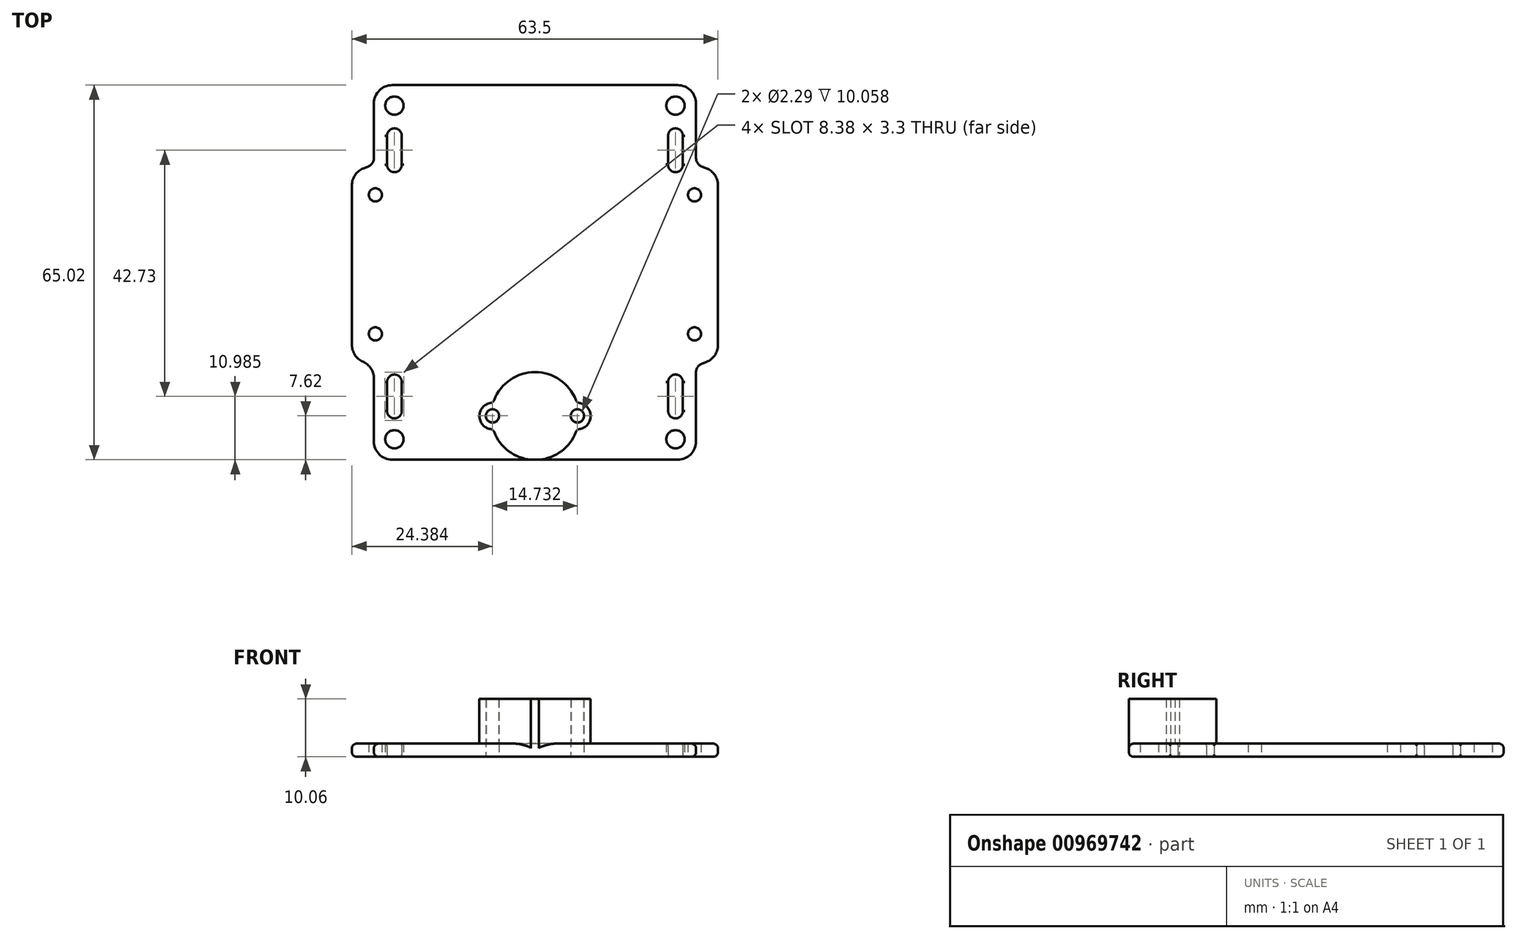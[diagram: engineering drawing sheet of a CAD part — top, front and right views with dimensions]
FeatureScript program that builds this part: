
annotation { "Feature Type Name" : "Feature", "Feature Type Description" : "" }
export const myFeature = defineFeature(function(context is Context, id is Id, definition is map)
    precondition{}
    {
        {
            var Q0;
            Q0=qCreatedBy(makeId("Top.planeOp"),FACE);
            var sketch = newSketch(context, id + "F0", { "sketchPlane" : qUnion([Q0])});
            skLineSegment(sketch, "E0", {"start": v(0, -32.35) * mm, "end": v(-27.94, -32.35) * mm});
            skLineSegment(sketch, "E1", {"start": v(-27.94, -32.35) * mm, "end": v(-27.94, -16.1) * mm});
            skLineSegment(sketch, "E2", {"start": v(-27.94, -16.1) * mm, "end": v(-31.75, -14.57) * mm});
            skLineSegment(sketch, "E3", {"start": v(-31.75, -14.57) * mm, "end": v(-31.75, 17.43) * mm});
            skLineSegment(sketch, "E4", {"start": v(-31.75, 17.43) * mm, "end": v(-27.94, 18.96) * mm});
            skLineSegment(sketch, "E5", {"start": v(-27.94, 18.96) * mm, "end": v(-27.94, 32.67) * mm});
            skLineSegment(sketch, "E6", {"start": v(-27.94, 32.67) * mm, "end": v(27.94, 32.67) * mm});
            skLineSegment(sketch, "E7", {"start": v(27.94, 32.67) * mm, "end": v(27.94, 18.96) * mm});
            skLineSegment(sketch, "E8", {"start": v(27.94, 18.96) * mm, "end": v(31.75, 17.43) * mm});
            skLineSegment(sketch, "E9", {"start": v(31.75, 17.43) * mm, "end": v(31.75, -14.57) * mm});
            skLineSegment(sketch, "E10", {"start": v(31.75, -14.57) * mm, "end": v(27.94, -16.1) * mm});
            skLineSegment(sketch, "E11", {"start": v(27.94, -16.1) * mm, "end": v(27.94, -32.35) * mm});
            skLineSegment(sketch, "E12", {"start": v(27.94, -32.35) * mm, "end": v(0, -32.35) * mm});
            skLineSegment(sketch, "E13", {"start": v(0, -32.35) * mm, "end": v(0, 32.67) * mm, "construction": true});
            skLineSegment(sketch, "E14", {"start": v(-29.38, 29.12) * mm, "end": v(30.41, 29.12) * mm, "construction": true});
            skLineSegment(sketch, "E15", {"start": v(-30.17, -28.8) * mm, "end": v(31.36, -28.8) * mm, "construction": true});
            skLineSegment(sketch, "E16", {"start": v(-24.38, 34.73) * mm, "end": v(-24.38, -35.44) * mm, "construction": true});
            skLineSegment(sketch, "E17", {"start": v(24.38, 35.22) * mm, "end": v(24.38, -36.91) * mm, "construction": true});
            skCircle(sketch, "E18", {"center": v(-24.38, 29.12) * mm, "radius": 1.59 * mm});
            skCircle(sketch, "E19", {"center": v(24.38, 29.12) * mm, "radius": 1.59 * mm});
            skCircle(sketch, "E20", {"center": v(-24.38, -28.8) * mm, "radius": 1.59 * mm});
            skCircle(sketch, "E21", {"center": v(24.38, -28.8) * mm, "radius": 1.59 * mm});
            skLineSegment(sketch, "E22", {"start": v(-27.69, 13.62) * mm, "end": v(-27.69, -10.5) * mm, "construction": true});
            skCircle(sketch, "E23", {"center": v(-27.69, 13.62) * mm, "radius": 1.14 * mm});
            skCircle(sketch, "E24", {"center": v(-27.69, -10.5) * mm, "radius": 1.14 * mm});
            skCircle(sketch, "E25.MirrorC", {"center": v(27.69, 13.62) * mm, "radius": 1.14 * mm});
            skCircle(sketch, "E26.MirrorC", {"center": v(27.69, -10.5) * mm, "radius": 1.14 * mm});
            skLineSegment(sketch, "E27", {"start": v(0, -24.73) * mm, "end": v(-7.37, -24.73) * mm});
            skCircle(sketch, "E28", {"center": v(0, -24.73) * mm, "radius": 7.62 * mm});
            skCircle(sketch, "E29", {"center": v(-7.37, -24.73) * mm, "radius": 1.14 * mm});
            skCircle(sketch, "E30", {"center": v(-7.37, -24.73) * mm, "radius": 2.29 * mm});
            skCircle(sketch, "E31.MirrorC", {"center": v(7.37, -24.73) * mm, "radius": 1.14 * mm});
            skCircle(sketch, "E32.MirrorC", {"center": v(7.37, -24.73) * mm, "radius": 2.29 * mm});
            skArc(sketch, "E33", {"start": v(-25.65, -23.85) * mm, "mid": v(-24.4, -25.17) * mm, "end": v(-23.11, -23.9) * mm});
            skArc(sketch, "E34", {"start": v(-23.12, -18.88) * mm, "mid": v(-24.38, -17.55) * mm, "end": v(-25.65, -18.88) * mm});
            skLineSegment(sketch, "E35", {"start": v(-25.65, -18.77) * mm, "end": v(-25.65, -23.96) * mm});
            skLineSegment(sketch, "E36", {"start": v(-23.12, -18.77) * mm, "end": v(-23.11, -23.9) * mm});
            skArc(sketch, "E37.MirrorCS", {"start": v(23.12, -18.88) * mm, "mid": v(24.38, -17.55) * mm, "end": v(25.65, -18.88) * mm});
            skArc(sketch, "E38.MirrorCS", {"start": v(25.65, -23.85) * mm, "mid": v(24.4, -25.17) * mm, "end": v(23.11, -23.9) * mm});
            skLineSegment(sketch, "E39.MirrorCS", {"start": v(23.12, -18.77) * mm, "end": v(23.11, -23.9) * mm});
            skLineSegment(sketch, "E40.MirrorCS", {"start": v(25.65, -18.77) * mm, "end": v(25.65, -23.96) * mm});
            skPoint(sketch, "E41.orphan", {"position": v(-24.38, -22.63) * mm});
            skPoint(sketch, "E42.orphan", {"position": v(24.38, -22.63) * mm});
            skArc(sketch, "E43.MirrorCS", {"start": v(23.12, 18.88) * mm, "mid": v(24.38, 17.55) * mm, "end": v(25.65, 18.88) * mm});
            skLineSegment(sketch, "E44.MirrorCS", {"start": v(23.12, 18.77) * mm, "end": v(23.11, 23.9) * mm});
            skArc(sketch, "E45.MirrorCS", {"start": v(25.65, 23.85) * mm, "mid": v(24.4, 25.17) * mm, "end": v(23.11, 23.9) * mm});
            skLineSegment(sketch, "E46.MirrorCS", {"start": v(25.65, 18.77) * mm, "end": v(25.65, 23.96) * mm});
            skArc(sketch, "E47.MirrorCS", {"start": v(-25.65, 23.85) * mm, "mid": v(-24.4, 25.17) * mm, "end": v(-23.11, 23.9) * mm});
            skLineSegment(sketch, "E48.MirrorCS", {"start": v(-23.12, 18.77) * mm, "end": v(-23.11, 23.9) * mm});
            skArc(sketch, "E49.MirrorCS", {"start": v(-23.12, 18.88) * mm, "mid": v(-24.38, 17.55) * mm, "end": v(-25.65, 18.88) * mm});
            skLineSegment(sketch, "E50.MirrorCS", {"start": v(-25.65, 18.77) * mm, "end": v(-25.65, 23.96) * mm});
            skSolve(sketch);
        }
        {
            var Q0;
            {var subQ6=sQuery(id+"F0.wireOp",EDGE,"E0");Q0=makeQuery(id+"F0.imprint","IMPRINT",FACE,{"disambiguationData":[TD([[makeQuery(id+"F0.imprint","IMPRINT",EDGE,{"derivedFrom":subQ6}),-1.0]])]});}
            var Q1;
            {var subQ2=sQuery(id+"F0.wireOp",EDGE,"E28");var subQ4=sQuery(id+"F0.wireOp",EDGE,"E32.MirrorC");var subQ5=makeQuery(id+"F0.imprint","INTERSECT",VERTEX,{"disambiguationData":[OD(0.0)],"derivedFrom":[subQ2,subQ4]});Q1=makeQuery(id+"F0.imprint","IMPRINT",FACE,{"disambiguationData":[TD([[makeQuery(id+"F0.imprint","IMPRINT",EDGE,{"disambiguationData":[TD([[subQ5,-1.0]])],"derivedFrom":subQ2}),1.0]])]});}
            var Q2;
            {var subQ0=sQuery(id+"F0.wireOp",EDGE,"E29");var subQ1=sQuery(id+"F0.wireOp",EDGE,"E27");var subQ2=makeQuery(id+"F0.imprint","INTERSECT",VERTEX,{"derivedFrom":[subQ1,subQ0]});Q2=makeQuery(id+"F0.imprint","IMPRINT",FACE,{"disambiguationData":[TD([[makeQuery(id+"F0.imprint","IMPRINT",EDGE,{"disambiguationData":[TD([[subQ2,1.0]])],"derivedFrom":subQ1}),-1.0]])]});}
            var Q3;
            {var subQ0=sQuery(id+"F0.wireOp",EDGE,"E30");var subQ1=sQuery(id+"F0.wireOp",EDGE,"E28");var subQ2=makeQuery(id+"F0.imprint","INTERSECT",VERTEX,{"disambiguationData":[OD(0.0)],"derivedFrom":[subQ1,subQ0]});Q3=makeQuery(id+"F0.imprint","IMPRINT",FACE,{"disambiguationData":[TD([[makeQuery(id+"F0.imprint","IMPRINT",EDGE,{"disambiguationData":[TD([[subQ2,-1.0]])],"derivedFrom":subQ1}),-1.0]])]});}
            var Q4;
            {var subQ0=sQuery(id+"F0.wireOp",EDGE,"E29");var subQ1=sQuery(id+"F0.wireOp",EDGE,"E27");var subQ2=makeQuery(id+"F0.imprint","INTERSECT",VERTEX,{"derivedFrom":[subQ1,subQ0]});Q4=makeQuery(id+"F0.imprint","IMPRINT",FACE,{"disambiguationData":[TD([[makeQuery(id+"F0.imprint","IMPRINT",EDGE,{"disambiguationData":[TD([[subQ2,1.0]])],"derivedFrom":subQ1}),1.0]])]});}
            var Q5;
            {var subQ0=sQuery(id+"F0.wireOp",EDGE,"E32.MirrorC");var subQ1=sQuery(id+"F0.wireOp",EDGE,"E28");var subQ2=makeQuery(id+"F0.imprint","INTERSECT",VERTEX,{"disambiguationData":[OD(0.0)],"derivedFrom":[subQ1,subQ0]});Q5=makeQuery(id+"F0.imprint","IMPRINT",FACE,{"disambiguationData":[TD([[makeQuery(id+"F0.imprint","IMPRINT",EDGE,{"disambiguationData":[TD([[subQ2,1.0]])],"derivedFrom":subQ1}),-1.0]])]});}
            var Q6;
            {var subQ0=sQuery(id+"F0.wireOp",EDGE,"E32.MirrorC");var subQ1=sQuery(id+"F0.wireOp",EDGE,"E28");var subQ2=makeQuery(id+"F0.imprint","INTERSECT",VERTEX,{"disambiguationData":[OD(0.0)],"derivedFrom":[subQ1,subQ0]});Q6=makeQuery(id+"F0.imprint","IMPRINT",FACE,{"disambiguationData":[TD([[makeQuery(id+"F0.imprint","IMPRINT",EDGE,{"disambiguationData":[TD([[subQ2,1.0]])],"derivedFrom":subQ1}),1.0]])]});}
            extrude(context, id + "F1", {"entities" : qUnion([Q0, Q1, Q2, Q3, Q4, Q5, Q6]), "depth" : 2.3 * mm, "offsetDistance" : 25.4 * mm});
        }
        {
            var Q0;
            Q0=makeQuery(id+"F1.opExtrude","CAP_FACE",FACE,{"disambiguationData":[OSD([sQuery(id+"F0.wireOp",EDGE,"E0"),sQuery(id+"F0.wireOp",EDGE,"E1"),sQuery(id+"F0.wireOp",EDGE,"E2"),sQuery(id+"F0.wireOp",EDGE,"E3"),sQuery(id+"F0.wireOp",EDGE,"E4"),sQuery(id+"F0.wireOp",EDGE,"E5"),sQuery(id+"F0.wireOp",EDGE,"E6"),sQuery(id+"F0.wireOp",EDGE,"E7"),sQuery(id+"F0.wireOp",EDGE,"E8"),sQuery(id+"F0.wireOp",EDGE,"E9"),sQuery(id+"F0.wireOp",EDGE,"E10"),sQuery(id+"F0.wireOp",EDGE,"E11"),sQuery(id+"F0.wireOp",EDGE,"E12"),sQuery(id+"F0.wireOp",EDGE,"E18"),sQuery(id+"F0.wireOp",EDGE,"E19"),sQuery(id+"F0.wireOp",EDGE,"E20"),sQuery(id+"F0.wireOp",EDGE,"E21"),sQuery(id+"F0.wireOp",EDGE,"E23"),sQuery(id+"F0.wireOp",EDGE,"E24"),sQuery(id+"F0.wireOp",EDGE,"E25.MirrorC"),sQuery(id+"F0.wireOp",EDGE,"E26.MirrorC"),sQuery(id+"F0.wireOp",EDGE,"E29"),sQuery(id+"F0.wireOp",EDGE,"E31.MirrorC")])],"isStart":false});
            var sketch = newSketch(context, id + "F2", { "sketchPlane" : qUnion([Q0])});
            skCircle(sketch, "E51", {"center": v(0.01, -24.76) * mm, "radius": 7.62 * mm});
            skCircle(sketch, "E52", {"center": v(-7.35, -24.76) * mm, "radius": 1.14 * mm});
            skCircle(sketch, "E53", {"center": v(-7.35, -24.76) * mm, "radius": 2.29 * mm});
            skCircle(sketch, "E54.MirrorC", {"center": v(7.38, -24.76) * mm, "radius": 1.14 * mm});
            skCircle(sketch, "E55.MirrorC", {"center": v(7.38, -24.76) * mm, "radius": 2.29 * mm});
            skSolve(sketch);
        }
        {
            var Q0;
            {var subQ1=sQuery(id+"F2.wireOp",EDGE,"E51");var subQ6=sQuery(id+"F2.wireOp",EDGE,"E53");var subQ8=makeQuery(id+"F2.imprint","INTERSECT",VERTEX,{"disambiguationData":[OD(0.0)],"derivedFrom":[subQ1,subQ6]});Q0=makeQuery(id+"F2.imprint","IMPRINT",FACE,{"disambiguationData":[TD([[makeQuery(id+"F2.imprint","IMPRINT",EDGE,{"disambiguationData":[TD([[subQ8,-1.0]])],"derivedFrom":subQ1}),-1.0]])]});}
            var Q1;
            {var subQ0=sQuery(id+"F2.wireOp",EDGE,"E53");var subQ1=sQuery(id+"F2.wireOp",EDGE,"E51");var subQ2=makeQuery(id+"F2.imprint","INTERSECT",VERTEX,{"disambiguationData":[OD(0.0)],"derivedFrom":[subQ1,subQ0]});Q1=makeQuery(id+"F2.imprint","IMPRINT",FACE,{"disambiguationData":[TD([[makeQuery(id+"F2.imprint","IMPRINT",EDGE,{"disambiguationData":[TD([[subQ2,-1.0]])],"derivedFrom":subQ1}),1.0]])]});}
            var Q2;
            {var subQ1=sQuery(id+"F2.wireOp",EDGE,"E51");var subQ6=sQuery(id+"F2.wireOp",EDGE,"E55.MirrorC");var subQ9=makeQuery(id+"F2.imprint","INTERSECT",VERTEX,{"disambiguationData":[OD(0.0)],"derivedFrom":[subQ1,subQ6]});Q2=makeQuery(id+"F2.imprint","IMPRINT",FACE,{"disambiguationData":[TD([[makeQuery(id+"F2.imprint","IMPRINT",EDGE,{"disambiguationData":[TD([[subQ9,-1.0]])],"derivedFrom":subQ1}),1.0]])]});}
            var Q3;
            {var subQ0=sQuery(id+"F2.wireOp",EDGE,"E55.MirrorC");var subQ1=sQuery(id+"F2.wireOp",EDGE,"E51");var subQ2=makeQuery(id+"F2.imprint","INTERSECT",VERTEX,{"disambiguationData":[OD(0.0)],"derivedFrom":[subQ1,subQ0]});Q3=makeQuery(id+"F2.imprint","IMPRINT",FACE,{"disambiguationData":[TD([[makeQuery(id+"F2.imprint","IMPRINT",EDGE,{"disambiguationData":[TD([[subQ2,1.0]])],"derivedFrom":subQ1}),1.0]])]});}
            var Q4;
            {var subQ0=sQuery(id+"F2.wireOp",EDGE,"E55.MirrorC");var subQ1=sQuery(id+"F2.wireOp",EDGE,"E51");var subQ2=makeQuery(id+"F2.imprint","INTERSECT",VERTEX,{"disambiguationData":[OD(0.0)],"derivedFrom":[subQ1,subQ0]});Q4=makeQuery(id+"F2.imprint","IMPRINT",FACE,{"disambiguationData":[TD([[makeQuery(id+"F2.imprint","IMPRINT",EDGE,{"disambiguationData":[TD([[subQ2,1.0]])],"derivedFrom":subQ1}),-1.0]])]});}
            extrude(context, id + "F3", {"entities" : qUnion([Q0, Q1, Q2, Q3, Q4]), "operationType" : NewBodyOperationType.ADD, "depth" : 7.77 * mm, "offsetDistance" : 25.4 * mm});
        }
        {
            var Q0;
            {var subQ0=sQuery(id+"F2.wireOp",EDGE,"E53");var subQ1=sQuery(id+"F2.wireOp",EDGE,"E51");Q0=makeQuery(id+"F3.opExtrude","SWEPT_EDGE",EDGE,{"disambiguationData":[OSD([subQ1,subQ0]),TDD([makeQuery(id+"F2.imprint","INTERSECT",VERTEX,{"disambiguationData":[OD(1.0)],"derivedFrom":[subQ1,subQ0]})])]});}
            var Q1;
            {var subQ0=sQuery(id+"F2.wireOp",EDGE,"E51");Q1=makeQuery(id+"F3.opExtrude","CAP_EDGE",EDGE,{"disambiguationData":[OSD([subQ0]),TDD([makeQuery(id+"F2.imprint","IMPRINT",EDGE,{"disambiguationData":[TD([[makeQuery(id+"F2.imprint","INTERSECT",VERTEX,{"disambiguationData":[OD(1.0)],"derivedFrom":[subQ0,sQuery(id+"F2.wireOp",EDGE,"E53")]}),-1.0]])],"derivedFrom":subQ0})])],"isStart":true});}
            var Q2;
            Q2=makeQuery(id+"F3.opExtrude","CAP_EDGE",EDGE,{"disambiguationData":[OSD([sQuery(id+"F2.wireOp",EDGE,"E53")])],"isStart":true});
            var Q3;
            {var subQ0=sQuery(id+"F2.wireOp",EDGE,"E53");var subQ1=sQuery(id+"F2.wireOp",EDGE,"E51");Q3=makeQuery(id+"F3.opExtrude","SWEPT_EDGE",EDGE,{"disambiguationData":[OSD([subQ1,subQ0]),TDD([makeQuery(id+"F2.imprint","INTERSECT",VERTEX,{"disambiguationData":[OD(0.0)],"derivedFrom":[subQ1,subQ0]})])]});}
            var Q4;
            {var subQ0=sQuery(id+"F2.wireOp",EDGE,"E51");Q4=makeQuery(id+"F3.opExtrude","CAP_EDGE",EDGE,{"disambiguationData":[OSD([subQ0]),TDD([makeQuery(id+"F2.imprint","IMPRINT",EDGE,{"disambiguationData":[TD([[makeQuery(id+"F2.imprint","INTERSECT",VERTEX,{"disambiguationData":[OD(0.0)],"derivedFrom":[subQ0,sQuery(id+"F2.wireOp",EDGE,"E55.MirrorC")]}),-1.0]])],"derivedFrom":subQ0})])],"isStart":true});}
            var Q5;
            {var subQ0=sQuery(id+"F2.wireOp",EDGE,"E55.MirrorC");var subQ1=sQuery(id+"F2.wireOp",EDGE,"E51");Q5=makeQuery(id+"F3.opExtrude","SWEPT_EDGE",EDGE,{"disambiguationData":[OSD([subQ1,subQ0]),TDD([makeQuery(id+"F2.imprint","INTERSECT",VERTEX,{"disambiguationData":[OD(0.0)],"derivedFrom":[subQ1,subQ0]})])]});}
            var Q6;
            Q6=makeQuery(id+"F3.opExtrude","CAP_EDGE",EDGE,{"disambiguationData":[OSD([sQuery(id+"F2.wireOp",EDGE,"E55.MirrorC")])],"isStart":true});
            var Q7;
            {var subQ0=sQuery(id+"F2.wireOp",EDGE,"E55.MirrorC");var subQ1=sQuery(id+"F2.wireOp",EDGE,"E51");Q7=makeQuery(id+"F3.opExtrude","SWEPT_EDGE",EDGE,{"disambiguationData":[OSD([subQ1,subQ0]),TDD([makeQuery(id+"F2.imprint","INTERSECT",VERTEX,{"disambiguationData":[OD(1.0)],"derivedFrom":[subQ1,subQ0]})])]});}
            var Q8;
            {var subQ0=sQuery(id+"F2.wireOp",EDGE,"E51");Q8=makeQuery(id+"F3.opExtrude","CAP_EDGE",EDGE,{"disambiguationData":[OSD([subQ0]),TDD([makeQuery(id+"F2.imprint","IMPRINT",EDGE,{"disambiguationData":[TD([[makeQuery(id+"F2.imprint","INTERSECT",VERTEX,{"disambiguationData":[OD(1.0)],"derivedFrom":[subQ0,sQuery(id+"F2.wireOp",EDGE,"E55.MirrorC")]}),1.0]])],"derivedFrom":subQ0})])],"isStart":true});}
            fillet(context, id + "F4", {"entities" : qUnion([Q0, Q1, Q2, Q3, Q4, Q5, Q6, Q7, Q8]), "radius" : 0.81 * mm, "tangentPropagation" : true, "allowEdgeOverflow" : false});
        }
        {
            var Q0;
            Q0=makeQuery(id+"F1.opExtrude","SWEPT_EDGE",EDGE,{"disambiguationData":[OSD([sQuery(id+"F0.wireOp",EDGE,"E6"),sQuery(id+"F0.wireOp",EDGE,"E7")])]});
            var Q1;
            Q1=makeQuery(id+"F1.opExtrude","SWEPT_EDGE",EDGE,{"disambiguationData":[OSD([sQuery(id+"F0.wireOp",EDGE,"E5"),sQuery(id+"F0.wireOp",EDGE,"E6")])]});
            var Q2;
            Q2=makeQuery(id+"F1.opExtrude","SWEPT_EDGE",EDGE,{"disambiguationData":[OSD([sQuery(id+"F0.wireOp",EDGE,"E0"),sQuery(id+"F0.wireOp",EDGE,"E1")])]});
            var Q3;
            Q3=makeQuery(id+"F1.opExtrude","SWEPT_EDGE",EDGE,{"disambiguationData":[OSD([sQuery(id+"F0.wireOp",EDGE,"E11"),sQuery(id+"F0.wireOp",EDGE,"E12")])]});
            var Q4;
            Q4=makeQuery(id+"F1.opExtrude","SWEPT_EDGE",EDGE,{"disambiguationData":[OSD([sQuery(id+"F0.wireOp",EDGE,"E2"),sQuery(id+"F0.wireOp",EDGE,"E3")])]});
            var Q5;
            Q5=makeQuery(id+"F1.opExtrude","SWEPT_EDGE",EDGE,{"disambiguationData":[OSD([sQuery(id+"F0.wireOp",EDGE,"E3"),sQuery(id+"F0.wireOp",EDGE,"E4")])]});
            var Q6;
            Q6=makeQuery(id+"F1.opExtrude","SWEPT_EDGE",EDGE,{"disambiguationData":[OSD([sQuery(id+"F0.wireOp",EDGE,"E9"),sQuery(id+"F0.wireOp",EDGE,"E10")])]});
            var Q7;
            Q7=makeQuery(id+"F1.opExtrude","SWEPT_EDGE",EDGE,{"disambiguationData":[OSD([sQuery(id+"F0.wireOp",EDGE,"E8"),sQuery(id+"F0.wireOp",EDGE,"E9")])]});
            fillet(context, id + "F5", {"entities" : qUnion([Q0, Q1, Q2, Q3, Q4, Q5, Q6, Q7]), "radius" : 3.17 * mm, "tangentPropagation" : true, "allowEdgeOverflow" : false});
        }
        {
            var Q0;
            Q0=makeQuery(id+"F1.opExtrude","SWEPT_EDGE",EDGE,{"disambiguationData":[OSD([sQuery(id+"F0.wireOp",EDGE,"E3"),sQuery(id+"F0.wireOp",EDGE,"E4")])]});
            var Q1;
            Q1=makeQuery(id+"F1.opExtrude","SWEPT_EDGE",EDGE,{"disambiguationData":[OSD([sQuery(id+"F0.wireOp",EDGE,"E1"),sQuery(id+"F0.wireOp",EDGE,"E2")])]});
            var Q2;
            Q2=makeQuery(id+"F1.opExtrude","SWEPT_EDGE",EDGE,{"disambiguationData":[OSD([sQuery(id+"F0.wireOp",EDGE,"E8"),sQuery(id+"F0.wireOp",EDGE,"E9")])]});
            var Q3;
            Q3=makeQuery(id+"F1.opExtrude","SWEPT_EDGE",EDGE,{"disambiguationData":[OSD([sQuery(id+"F0.wireOp",EDGE,"E9"),sQuery(id+"F0.wireOp",EDGE,"E10")])]});
            fillet(context, id + "F6", {"entities" : qUnion([Q0, Q1, Q2, Q3]), "radius" : 3.17 * mm, "tangentPropagation" : true, "allowEdgeOverflow" : false});
        }
        {
            var Q0;
            Q0=makeQuery(id+"F1.opExtrude","SWEPT_EDGE",EDGE,{"disambiguationData":[OSD([sQuery(id+"F0.wireOp",EDGE,"E4"),sQuery(id+"F0.wireOp",EDGE,"E5")])]});
            var Q1;
            Q1=makeQuery(id+"F1.opExtrude","SWEPT_EDGE",EDGE,{"disambiguationData":[OSD([sQuery(id+"F0.wireOp",EDGE,"E7"),sQuery(id+"F0.wireOp",EDGE,"E8")])]});
            var Q2;
            Q2=makeQuery(id+"F1.opExtrude","SWEPT_EDGE",EDGE,{"disambiguationData":[OSD([sQuery(id+"F0.wireOp",EDGE,"E10"),sQuery(id+"F0.wireOp",EDGE,"E11")])]});
            fillet(context, id + "F7", {"entities" : qUnion([Q0, Q1, Q2]), "radius" : 1.57 * mm, "tangentPropagation" : true, "allowEdgeOverflow" : false});
        }
        {
            var Q0;
            Q0=makeQuery(id+"F1.opExtrude","SWEPT_FACE",FACE,{"disambiguationData":[OSD([sQuery(id+"F0.wireOp",EDGE,"E9")])]});
            fillet(context, id + "F8", {"entities" : qUnion([Q0]), "radius" : 0.81 * mm, "tangentPropagation" : true, "allowEdgeOverflow" : false});
        }
        {
            var Q0;
            Q0=makeQuery(id+"F1.opExtrude","CAP_EDGE",EDGE,{"disambiguationData":[OSD([sQuery(id+"F0.wireOp",EDGE,"E44.MirrorCS")])],"isStart":false});
            var Q1;
            Q1=makeQuery(id+"F1.opExtrude","CAP_EDGE",EDGE,{"disambiguationData":[OSD([sQuery(id+"F0.wireOp",EDGE,"E43.MirrorCS")])],"isStart":false});
            var Q2;
            Q2=makeQuery(id+"F1.opExtrude","CAP_EDGE",EDGE,{"disambiguationData":[OSD([sQuery(id+"F0.wireOp",EDGE,"E46.MirrorCS")])],"isStart":false});
            var Q3;
            Q3=makeQuery(id+"F1.opExtrude","CAP_EDGE",EDGE,{"disambiguationData":[OSD([sQuery(id+"F0.wireOp",EDGE,"E47.MirrorCS")])],"isStart":false});
            var Q4;
            Q4=makeQuery(id+"F1.opExtrude","CAP_EDGE",EDGE,{"disambiguationData":[OSD([sQuery(id+"F0.wireOp",EDGE,"E48.MirrorCS")])],"isStart":false});
            var Q5;
            Q5=makeQuery(id+"F1.opExtrude","CAP_EDGE",EDGE,{"disambiguationData":[OSD([sQuery(id+"F0.wireOp",EDGE,"E49.MirrorCS")])],"isStart":false});
            var Q6;
            Q6=makeQuery(id+"F1.opExtrude","CAP_EDGE",EDGE,{"disambiguationData":[OSD([sQuery(id+"F0.wireOp",EDGE,"E50.MirrorCS")])],"isStart":false});
            var Q7;
            Q7=makeQuery(id+"F1.opExtrude","CAP_EDGE",EDGE,{"disambiguationData":[OSD([sQuery(id+"F0.wireOp",EDGE,"E36")])],"isStart":false});
            var Q8;
            Q8=makeQuery(id+"F1.opExtrude","CAP_EDGE",EDGE,{"disambiguationData":[OSD([sQuery(id+"F0.wireOp",EDGE,"E34")])],"isStart":false});
            var Q9;
            Q9=makeQuery(id+"F1.opExtrude","CAP_EDGE",EDGE,{"disambiguationData":[OSD([sQuery(id+"F0.wireOp",EDGE,"E35")])],"isStart":false});
            var Q10;
            Q10=makeQuery(id+"F1.opExtrude","CAP_EDGE",EDGE,{"disambiguationData":[OSD([sQuery(id+"F0.wireOp",EDGE,"E33")])],"isStart":false});
            var Q11;
            Q11=makeQuery(id+"F1.opExtrude","CAP_EDGE",EDGE,{"disambiguationData":[OSD([sQuery(id+"F0.wireOp",EDGE,"E37.MirrorCS")])],"isStart":false});
            var Q12;
            Q12=makeQuery(id+"F1.opExtrude","CAP_EDGE",EDGE,{"disambiguationData":[OSD([sQuery(id+"F0.wireOp",EDGE,"E40.MirrorCS")])],"isStart":false});
            var Q13;
            Q13=makeQuery(id+"F1.opExtrude","CAP_EDGE",EDGE,{"disambiguationData":[OSD([sQuery(id+"F0.wireOp",EDGE,"E39.MirrorCS")])],"isStart":false});
            var Q14;
            Q14=makeQuery(id+"F1.opExtrude","CAP_EDGE",EDGE,{"disambiguationData":[OSD([sQuery(id+"F0.wireOp",EDGE,"E38.MirrorCS")])],"isStart":false});
            var Q15;
            Q15=makeQuery(id+"F1.opExtrude","CAP_EDGE",EDGE,{"disambiguationData":[OSD([sQuery(id+"F0.wireOp",EDGE,"E49.MirrorCS")])],"isStart":true});
            var Q16;
            Q16=makeQuery(id+"F1.opExtrude","CAP_EDGE",EDGE,{"disambiguationData":[OSD([sQuery(id+"F0.wireOp",EDGE,"E50.MirrorCS")])],"isStart":true});
            var Q17;
            Q17=makeQuery(id+"F1.opExtrude","CAP_EDGE",EDGE,{"disambiguationData":[OSD([sQuery(id+"F0.wireOp",EDGE,"E47.MirrorCS")])],"isStart":true});
            var Q18;
            Q18=makeQuery(id+"F1.opExtrude","CAP_EDGE",EDGE,{"disambiguationData":[OSD([sQuery(id+"F0.wireOp",EDGE,"E43.MirrorCS")])],"isStart":true});
            var Q19;
            Q19=makeQuery(id+"F1.opExtrude","CAP_EDGE",EDGE,{"disambiguationData":[OSD([sQuery(id+"F0.wireOp",EDGE,"E46.MirrorCS")])],"isStart":true});
            var Q20;
            Q20=makeQuery(id+"F1.opExtrude","CAP_EDGE",EDGE,{"disambiguationData":[OSD([sQuery(id+"F0.wireOp",EDGE,"E45.MirrorCS")])],"isStart":true});
            var Q21;
            Q21=makeQuery(id+"F1.opExtrude","CAP_EDGE",EDGE,{"disambiguationData":[OSD([sQuery(id+"F0.wireOp",EDGE,"E35")])],"isStart":true});
            var Q22;
            Q22=makeQuery(id+"F1.opExtrude","CAP_EDGE",EDGE,{"disambiguationData":[OSD([sQuery(id+"F0.wireOp",EDGE,"E33")])],"isStart":true});
            var Q23;
            Q23=makeQuery(id+"F1.opExtrude","CAP_EDGE",EDGE,{"disambiguationData":[OSD([sQuery(id+"F0.wireOp",EDGE,"E36")])],"isStart":true});
            var Q24;
            Q24=makeQuery(id+"F1.opExtrude","CAP_EDGE",EDGE,{"disambiguationData":[OSD([sQuery(id+"F0.wireOp",EDGE,"E34")])],"isStart":true});
            var Q25;
            Q25=makeQuery(id+"F1.opExtrude","CAP_EDGE",EDGE,{"disambiguationData":[OSD([sQuery(id+"F0.wireOp",EDGE,"E39.MirrorCS")])],"isStart":true});
            var Q26;
            Q26=makeQuery(id+"F1.opExtrude","CAP_EDGE",EDGE,{"disambiguationData":[OSD([sQuery(id+"F0.wireOp",EDGE,"E38.MirrorCS")])],"isStart":true});
            var Q27;
            Q27=makeQuery(id+"F1.opExtrude","CAP_EDGE",EDGE,{"disambiguationData":[OSD([sQuery(id+"F0.wireOp",EDGE,"E40.MirrorCS")])],"isStart":true});
            var Q28;
            Q28=makeQuery(id+"F1.opExtrude","CAP_EDGE",EDGE,{"disambiguationData":[OSD([sQuery(id+"F0.wireOp",EDGE,"E37.MirrorCS")])],"isStart":true});
            fillet(context, id + "F9", {"entities" : qUnion([Q0, Q1, Q2, Q3, Q4, Q5, Q6, Q7, Q8, Q9, Q10, Q11, Q12, Q13, Q14, Q15, Q16, Q17, Q18, Q19, Q20, Q21, Q22, Q23, Q24, Q25, Q26, Q27, Q28]), "radius" : 0.38 * mm, "tangentPropagation" : true, "allowEdgeOverflow" : false});
        }
    });
